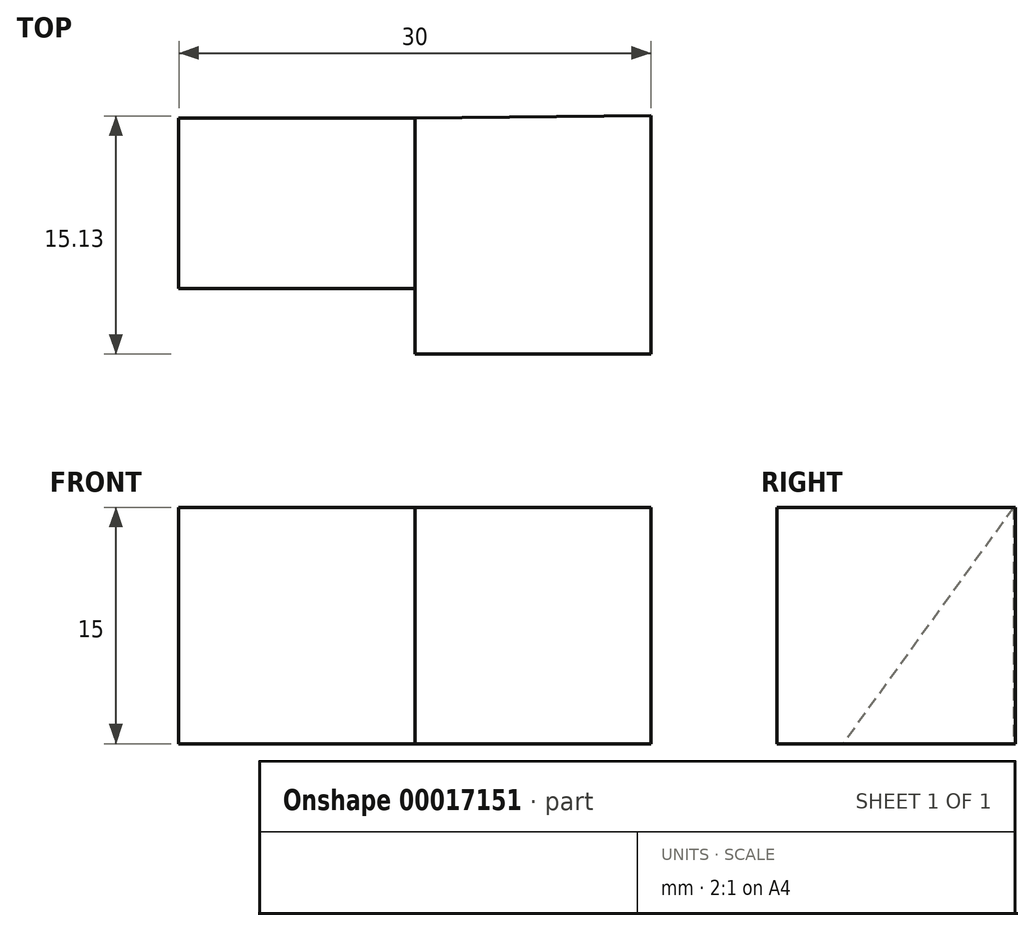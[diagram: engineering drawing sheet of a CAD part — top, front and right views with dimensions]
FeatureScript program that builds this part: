
annotation { "Feature Type Name" : "Feature", "Feature Type Description" : "" }
export const myFeature = defineFeature(function(context is Context, id is Id, definition is map)
    precondition{}
    {
        {
            var Q0;
            Q0=qCreatedBy(makeId("Top.planeOp"),FACE);
            var sketch = newSketch(context, id + "F0", { "sketchPlane" : qUnion([Q0])});
            skLineSegment(sketch, "E0", {"start": v(-19.77, 10.83) * mm, "end": v(-19.77, -4.17) * mm});
            skLineSegment(sketch, "E1", {"start": v(-19.77, -4.17) * mm, "end": v(-4.77, -4.17) * mm});
            skLineSegment(sketch, "E2", {"start": v(-4.77, -4.17) * mm, "end": v(-4.77, 10.96) * mm});
            skLineSegment(sketch, "E3", {"start": v(-4.77, 10.96) * mm, "end": v(-19.77, 10.83) * mm});
            skSolve(sketch);
        }
        {
            var Q0;
            Q0 = qSketchRegion(id + "F0", true);
            extrude(context, id + "F1", {"entities" : qUnion([Q0]), "depth" : 15 * mm});
        }
        {
            var Q0;
            Q0 = qSketchRegion(id + "F0", true);
            extrude(context, id + "F2", {"entities" : qUnion([Q0]), "operationType" : NewBodyOperationType.ADD, "depth" : 15 * mm});
        }
        {
            var Q0;
            Q0=makeQuery(id+"F1.opExtrude","SWEPT_FACE",FACE,{"disambiguationData":[OSD([sQuery(id+"F0.wireOp",EDGE,"E0")])]});
            var sketch = newSketch(context, id + "F3", { "sketchPlane" : qUnion([Q0])});
            skLineSegment(sketch, "E4", {"start": v(0, 0) * mm, "end": v(-10.83, 0) * mm});
            skLineSegment(sketch, "E5", {"start": v(-10.83, 0) * mm, "end": v(-10.83, 15) * mm});
            skLineSegment(sketch, "E6", {"start": v(-10.83, 15) * mm, "end": v(0, 0) * mm});
            skSolve(sketch);
        }
        {
            var Q0;
            Q0=makeQuery(id+"F3.imprint","IMPRINT",FACE,{"disambiguationData":[TD([[makeQuery(id+"F3.imprint","IMPRINT",EDGE,{"derivedFrom":sQuery(id+"F3.wireOp",EDGE,"E4")}),1.0]])]});
            extrude(context, id + "F4", {"entities" : qUnion([Q0]), "operationType" : NewBodyOperationType.ADD, "depth" : 15 * mm});
        }
    });
